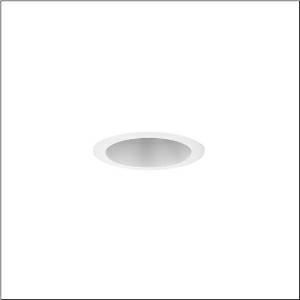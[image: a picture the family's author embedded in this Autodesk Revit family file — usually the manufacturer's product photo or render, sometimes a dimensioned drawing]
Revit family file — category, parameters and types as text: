
# Revit family: lunis_31_mini_51dn157e41
name_source: partatom
category: Lighting Fixtures
units: mm (PartAtom-declared; Revit-internal decimal feet)

## family parameters
Cut with Voids When Loaded = No
Host = Face
Light Source = No
Part Type = Normal
Room Calculation Point = No
Round Connector Dimension = Use Diameter
Shared = No

## types (1)
- Lunis 31 mini (1 x LED, 1040 lm, 8.3 W, 4000K)
    Apparent Load = 8 VA
    CIE Flux Codes = 93 98 100 100 100
    Color Rendering = 80
    Color Temperature = 4000K
    Default Elevation = 1800 mm
    Description = Lunis 31,  mini, downlight, light control with reflector, light emission: direct distribution, LED rated luminous flux: 1.040lm, light colour: 840, control gear: ECG, mains connection: 220..240V, AC, 50/60Hz, housing, white, protection rating (complete): IP20, insulation class (complete): insulation class II (safety insulation), certification: CE, packaging unit: 1 piece
    Height = 0 mm  [stored 0 ft]
    Lamp = 1 x LED
    Lamp Light Flux = 1040 lm
    Lamp Power = 8.3 W
    Lamp count = 1
    Length = 188 mm  [stored 0.616798 ft]
    Luminous efficacy = 125 lm/W
    Manufacturer = Siteco
    ModVariant = No
    Model = 51DN157E41
    Mounting Place = Ceiling
    Mounting Type = Recessed
    Number of Poles = 1
    OnlyDefault = Yes
    Power Factor = 1
    Product Name = Lunis 31 mini
    Product group = downlight | ceiling recessed
    ProductGroupID = 402
    Protection Class = Protection class II
    Protection Degree = IP 20
    RLX_Detail_Level = 1
    RlxData = <blob elided: 21769 chars, md5=32d35bf4>
    Socket = socket
    Standby Power = 0 W
    System Light Flux = 1040 lm
    System Power = 8 W
    Type Comments = Product without accessories
    Type Image = l_1005624.jpg
    URL = http://relux.com
    VarID = ---
    Voltage = 0 V
    Weight = 0.00 kg
    Width = 0 mm  [stored 0 ft]

note: [stored X ft] marks values corroborated as IEEE doubles in the binary element streams (Revit-internal decimal feet)

## geometry (parser evidence)
native form markers: Blend x4, Sweep x12
no freeform markers — native parametric forms only
